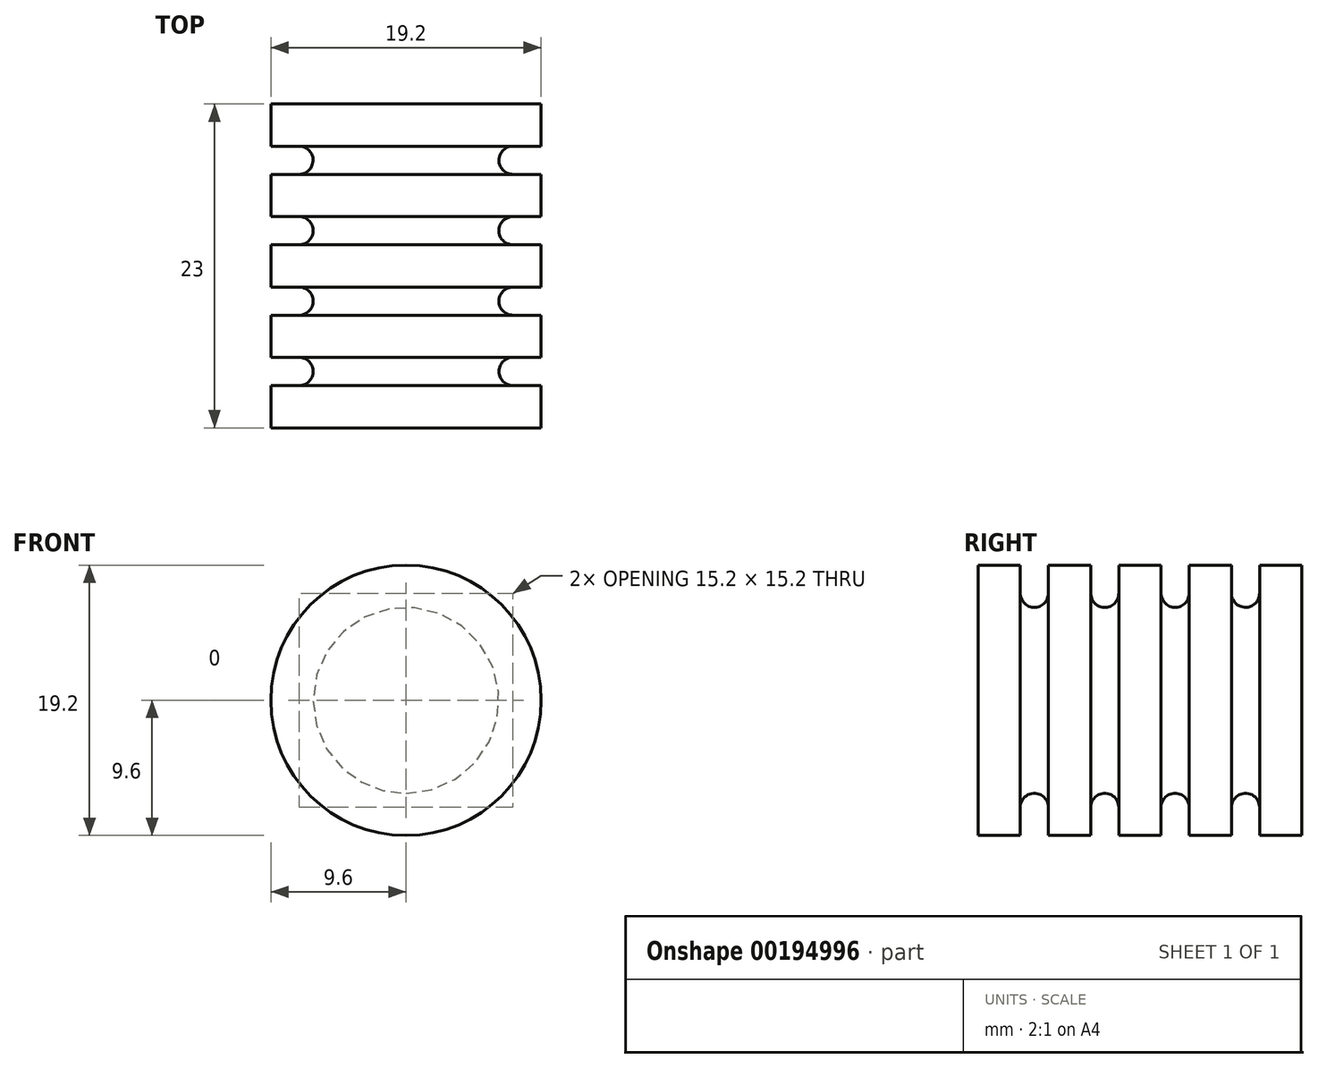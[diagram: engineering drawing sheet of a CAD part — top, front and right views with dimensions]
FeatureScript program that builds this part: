
annotation { "Feature Type Name" : "Feature", "Feature Type Description" : "" }
export const myFeature = defineFeature(function(context is Context, id is Id, definition is map)
    precondition{}
    {
        {
            var Q0;
            Q0=qCreatedBy(makeId("Top.planeOp"),FACE);
            var sketch = newSketch(context, id + "F0", { "sketchPlane" : qUnion([Q0])});
            skLineSegment(sketch, "E0", {"start": v(0, 0) * mm, "end": v(0, 23) * mm});
            skLineSegment(sketch, "E1", {"start": v(0, 0) * mm, "end": v(9.6, 0) * mm});
            skLineSegment(sketch, "E2", {"start": v(9.6, 0) * mm, "end": v(9.6, 3) * mm});
            skLineSegment(sketch, "E3", {"start": v(9.6, 3) * mm, "end": v(6.6, 3) * mm});
            skLineSegment(sketch, "E4", {"start": v(6.6, 3) * mm, "end": v(6.6, 5) * mm});
            skLineSegment(sketch, "E5", {"start": v(6.6, 5) * mm, "end": v(9.6, 5) * mm});
            skLineSegment(sketch, "E6", {"start": v(9.6, 5) * mm, "end": v(9.6, 8) * mm});
            skLineSegment(sketch, "E7.1.0.0", {"start": v(9.6, 8) * mm, "end": v(6.6, 8) * mm});
            skLineSegment(sketch, "E7.1.0.1", {"start": v(6.6, 8) * mm, "end": v(6.6, 10) * mm});
            skLineSegment(sketch, "E7.1.0.2", {"start": v(6.6, 10) * mm, "end": v(9.6, 10) * mm});
            skLineSegment(sketch, "E7.1.0.3", {"start": v(9.6, 10) * mm, "end": v(9.6, 13) * mm});
            skLineSegment(sketch, "E7.2.0.0", {"start": v(9.6, 13) * mm, "end": v(6.6, 13) * mm});
            skLineSegment(sketch, "E7.2.0.1", {"start": v(6.6, 13) * mm, "end": v(6.6, 15) * mm});
            skLineSegment(sketch, "E7.2.0.2", {"start": v(6.6, 15) * mm, "end": v(9.6, 15) * mm});
            skLineSegment(sketch, "E7.2.0.3", {"start": v(9.6, 15) * mm, "end": v(9.6, 18) * mm});
            skLineSegment(sketch, "E7.3.0.0", {"start": v(9.6, 18) * mm, "end": v(6.6, 18) * mm});
            skLineSegment(sketch, "E7.3.0.1", {"start": v(6.6, 18) * mm, "end": v(6.6, 20) * mm});
            skLineSegment(sketch, "E7.3.0.2", {"start": v(6.6, 20) * mm, "end": v(9.6, 20) * mm});
            skLineSegment(sketch, "E7.3.0.3", {"start": v(9.6, 20) * mm, "end": v(9.6, 23) * mm});
            skLineSegment(sketch, "E7.direction1", {"start": v(9.6, 3) * mm, "end": v(9.6, 8) * mm, "construction": true});
            skLineSegment(sketch, "E8", {"start": v(0, 23) * mm, "end": v(9.6, 23) * mm});
            skSolve(sketch);
        }
        {
            var Q0;
            Q0=makeQuery(id+"F0.imprint","IMPRINT",FACE,{"disambiguationData":[TD([[makeQuery(id+"F0.imprint","IMPRINT",EDGE,{"derivedFrom":sQuery(id+"F0.wireOp",EDGE,"E0")}),-1.0]])]});
            var Q1;
            Q1=sQuery(id+"F0.wireOp",EDGE,"E0");
            revolve(context, id + "F1", {"entities" : qUnion([Q0]), "axis" : qUnion([Q1]), "revolveType" : RevolveType.FULL});
        }
        {
            var Q0;
            Q0=makeQuery(id+"F1.opRevolve","SWEPT_EDGE",EDGE,{"disambiguationData":[OSD([sQuery(id+"F0.wireOp",EDGE,"E7.3.0.1"),sQuery(id+"F0.wireOp",EDGE,"E7.3.0.2")])]});
            var Q1;
            Q1=makeQuery(id+"F1.opRevolve","SWEPT_EDGE",EDGE,{"disambiguationData":[OSD([sQuery(id+"F0.wireOp",EDGE,"E7.4.0.1"),sQuery(id+"F0.wireOp",EDGE,"E7.4.0.2")])]});
            var Q2;
            Q2=makeQuery(id+"F1.opRevolve","SWEPT_EDGE",EDGE,{"disambiguationData":[OSD([sQuery(id+"F0.wireOp",EDGE,"E7.2.0.1"),sQuery(id+"F0.wireOp",EDGE,"E7.2.0.2")])]});
            var Q3;
            Q3=makeQuery(id+"F1.opRevolve","SWEPT_EDGE",EDGE,{"disambiguationData":[OSD([sQuery(id+"F0.wireOp",EDGE,"E7.1.0.1"),sQuery(id+"F0.wireOp",EDGE,"E7.1.0.2")])]});
            var Q4;
            Q4=makeQuery(id+"F1.opRevolve","SWEPT_EDGE",EDGE,{"disambiguationData":[OSD([sQuery(id+"F0.wireOp",EDGE,"E4"),sQuery(id+"F0.wireOp",EDGE,"E5")])]});
            var Q5;
            Q5=makeQuery(id+"F1.opRevolve","SWEPT_EDGE",EDGE,{"disambiguationData":[OSD([sQuery(id+"F0.wireOp",EDGE,"E3"),sQuery(id+"F0.wireOp",EDGE,"E4")])]});
            var Q6;
            Q6=makeQuery(id+"F1.opRevolve","SWEPT_EDGE",EDGE,{"disambiguationData":[OSD([sQuery(id+"F0.wireOp",EDGE,"E7.1.0.0"),sQuery(id+"F0.wireOp",EDGE,"E7.1.0.1")])]});
            var Q7;
            Q7=makeQuery(id+"F1.opRevolve","SWEPT_EDGE",EDGE,{"disambiguationData":[OSD([sQuery(id+"F0.wireOp",EDGE,"E7.2.0.0"),sQuery(id+"F0.wireOp",EDGE,"E7.2.0.1")])]});
            var Q8;
            Q8=makeQuery(id+"F1.opRevolve","SWEPT_EDGE",EDGE,{"disambiguationData":[OSD([sQuery(id+"F0.wireOp",EDGE,"E7.3.0.0"),sQuery(id+"F0.wireOp",EDGE,"E7.3.0.1")])]});
            var Q9;
            Q9=makeQuery(id+"F1.opRevolve","SWEPT_EDGE",EDGE,{"disambiguationData":[OSD([sQuery(id+"F0.wireOp",EDGE,"E7.4.0.0"),sQuery(id+"F0.wireOp",EDGE,"E7.4.0.1")])]});
            fillet(context, id + "F2", {"entities" : qUnion([Q0, Q1, Q2, Q3, Q4, Q5, Q6, Q7, Q8, Q9]), "radius" : 1 * mm, "tangentPropagation" : true, "allowEdgeOverflow" : false});
        }
    });
